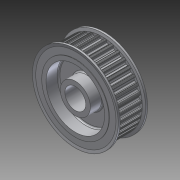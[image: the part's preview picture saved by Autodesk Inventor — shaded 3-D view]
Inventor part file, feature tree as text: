
AUTODESK INVENTOR PART (.ipt)
format: ipt  version: 2014 SP1 (Build 180222100, 222)  size: 1,108,992 bytes
history: native  units: in
note: dims shown in document units (in); Inventor stores cm internally (conversion verified against a paired STEP export)
features: mirror x1, other x1, extrude x1, imported_body x1, sketch x1
ambient origin geometry x8: Origin, YZ Plane, XZ Plane, XY Plane, X Axis, Y Axis, Z Axis, Center Point
bodies: Body1 (feature_tree)
feature tree (5):
  mirror  "Mirror1"
  other  "217-3232-STEP1"
  extrude  "Extrusion1"  [1 undecoded]
  imported_body  "Base1"
  sketch  "Sketch1"  dims[d0=39.3701in d1=0.0in]
note: 1 required parameter value undecoded (feature->parameter linkage not recoverable at this tier; creation-order binding heuristic only, values carry confidence <= 0.55)
